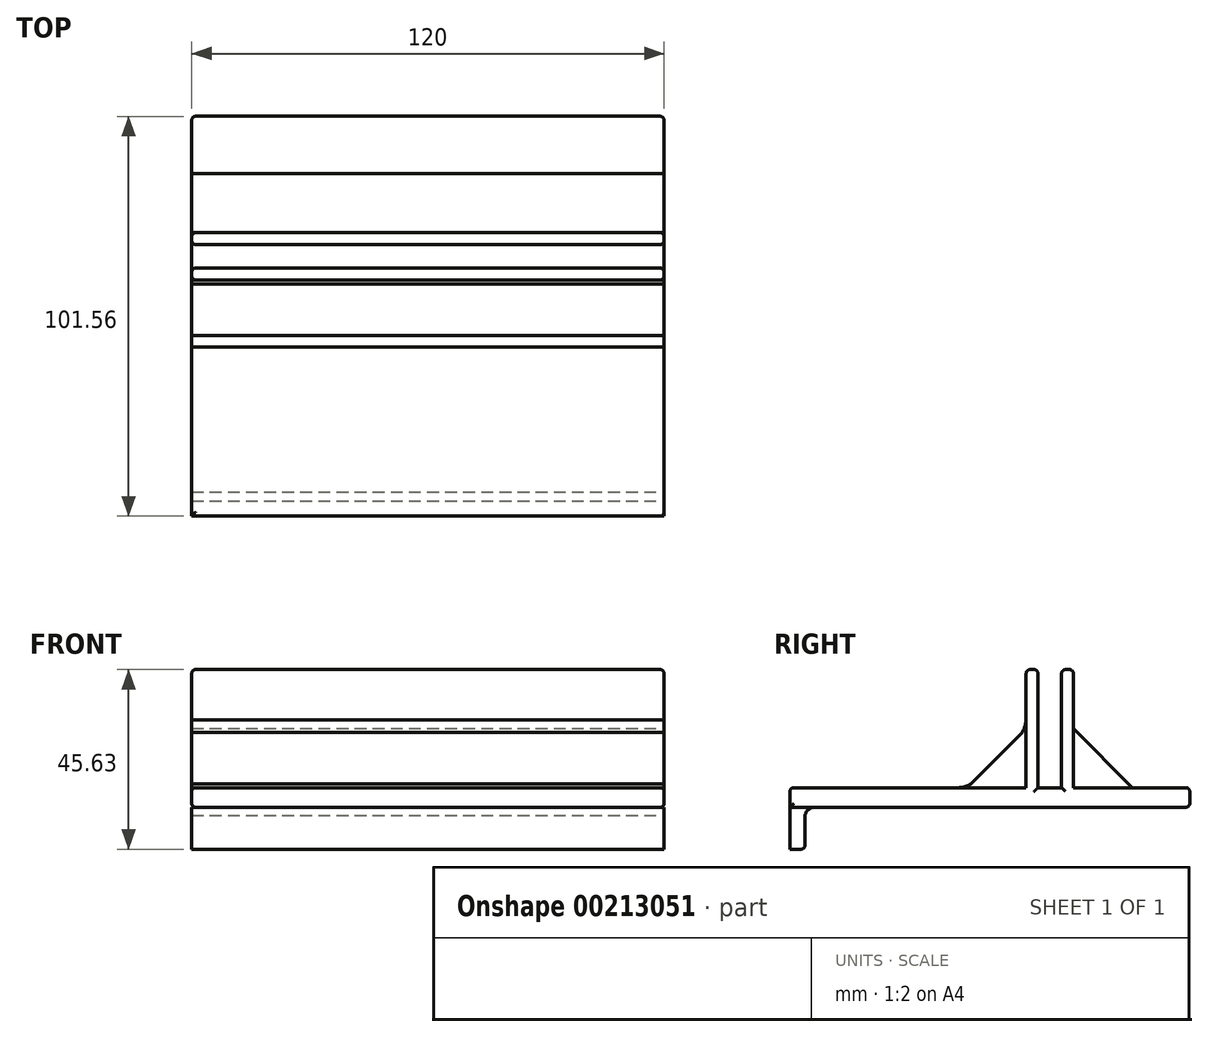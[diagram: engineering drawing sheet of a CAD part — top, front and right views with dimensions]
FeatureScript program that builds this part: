
annotation { "Feature Type Name" : "Feature", "Feature Type Description" : "" }
export const myFeature = defineFeature(function(context is Context, id is Id, definition is map)
    precondition{}
    {
        {
            var Q0;
            Q0=qCreatedBy(makeId("Top.planeOp"),FACE);
            var sketch = newSketch(context, id + "F0", { "sketchPlane" : qUnion([Q0])});
            skLineSegment(sketch, "E0.bottom", {"start": v(60, 66) * mm, "end": v(-60, 66) * mm});
            skLineSegment(sketch, "E0.top", {"start": v(60, -66) * mm, "end": v(-60, -66) * mm});
            skLineSegment(sketch, "E0.left", {"start": v(60, 66) * mm, "end": v(60, -66) * mm});
            skLineSegment(sketch, "E0.right", {"start": v(-60, 66) * mm, "end": v(-60, -66) * mm});
            skPoint(sketch, "E0.middle", {"position": v(0, 0) * mm});
            skSolve(sketch);
        }
        {
            var Q0;
            Q0=makeQuery(id+"F0.imprint","IMPRINT",FACE,{"disambiguationData":[TD([[makeQuery(id+"F0.imprint","IMPRINT",EDGE,{"derivedFrom":sQuery(id+"F0.wireOp",EDGE,"E0.bottom")}),1.0]])]});
            extrude(context, id + "F1", {"entities" : qUnion([Q0]), "depth" : 5 * mm});
        }
        {
            var Q0;
            Q0=makeQuery(id+"F1.opExtrude","CAP_FACE",FACE,{"disambiguationData":[OSD([sQuery(id+"F0.wireOp",EDGE,"E0.bottom"),sQuery(id+"F0.wireOp",EDGE,"E0.top"),sQuery(id+"F0.wireOp",EDGE,"E0.left"),sQuery(id+"F0.wireOp",EDGE,"E0.right")])],"isStart":false});
            var sketch = newSketch(context, id + "F2", { "sketchPlane" : qUnion([Q0])});
            skLineSegment(sketch, "E1.bottom", {"start": v(60, 6) * mm, "end": v(-60, 6) * mm});
            skLineSegment(sketch, "E1.top", {"start": v(60, -6) * mm, "end": v(-60, -6) * mm});
            skLineSegment(sketch, "E1.left", {"start": v(60, 6) * mm, "end": v(60, -6) * mm});
            skLineSegment(sketch, "E1.right", {"start": v(-60, 6) * mm, "end": v(-60, -6) * mm});
            skPoint(sketch, "E1.middle", {"position": v(0, 0) * mm});
            skLineSegment(sketch, "E2", {"start": v(-60, 3) * mm, "end": v(60, 3) * mm});
            skLineSegment(sketch, "E3", {"start": v(-60, -3) * mm, "end": v(60, -3) * mm});
            skSolve(sketch);
        }
        {
            var Q0;
            {var subQ0=sQuery(id+"F2.wireOp",EDGE,"E1.bottom");Q0=makeQuery(id+"F2.imprint","IMPRINT",FACE,{"disambiguationData":[TD([[makeQuery(id+"F2.imprint","IMPRINT",EDGE,{"derivedFrom":subQ0}),1.0]])]});}
            var Q1;
            {var subQ0=sQuery(id+"F2.wireOp",EDGE,"E1.top");Q1=makeQuery(id+"F2.imprint","IMPRINT",FACE,{"disambiguationData":[TD([[makeQuery(id+"F2.imprint","IMPRINT",EDGE,{"derivedFrom":subQ0}),-1.0]])]});}
            extrude(context, id + "F3", {"entities" : qUnion([Q0, Q1]), "operationType" : NewBodyOperationType.ADD, "depth" : 30 * mm});
        }
        {
            var Q0;
            {var subQ0=sQuery(id+"F2.wireOp",EDGE,"E1.left");var subQ1=sQuery(id+"F0.wireOp",EDGE,"E0.left");Q0=makeQuery(id+"F3.boolean.opBoolean","MERGE",FACE,{"derivedFrom":[makeQuery(id+"F1.opExtrude","SWEPT_FACE",FACE,{"disambiguationData":[OSD([subQ1])]}),makeQuery(id+"F3.opExtrude","SWEPT_FACE",FACE,{"disambiguationData":[OSD([subQ0]),TDD([makeQuery(id+"F2.imprint","IMPRINT",EDGE,{"disambiguationData":[TD([[makeQuery(id+"F2.imprint","INTERSECT",VERTEX,{"derivedFrom":[subQ0,sQuery(id+"F2.wireOp",EDGE,"E2")]}),1.0]])],"derivedFrom":subQ0})])]}),makeQuery(id+"F3.opExtrude","SWEPT_FACE",FACE,{"disambiguationData":[OSD([subQ0]),TDD([makeQuery(id+"F2.imprint","IMPRINT",EDGE,{"disambiguationData":[TD([[makeQuery(id+"F2.imprint","INTERSECT",VERTEX,{"derivedFrom":[subQ0,sQuery(id+"F2.wireOp",EDGE,"E3")]}),-1.0]])],"derivedFrom":subQ0})])]})]});}
            var sketch = newSketch(context, id + "F4", { "sketchPlane" : qUnion([Q0])});
            skLineSegment(sketch, "E4", {"start": v(-21, 5) * mm, "end": v(-6, 20) * mm});
            skLineSegment(sketch, "E5", {"start": v(21, 5) * mm, "end": v(6, 20) * mm});
            skLineSegment(sketch, "E6.bottom", {"start": v(-66, 0) * mm, "end": v(-62.19, 0) * mm});
            skLineSegment(sketch, "E6.top", {"start": v(-66, -10.63) * mm, "end": v(-62.19, -10.63) * mm});
            skLineSegment(sketch, "E6.left", {"start": v(-66, 0) * mm, "end": v(-66, -10.63) * mm});
            skLineSegment(sketch, "E6.right", {"start": v(-62.19, 0) * mm, "end": v(-62.19, -10.63) * mm});
            skArc(sketch, "E7", {"start": v(-7.02, 18.98) * mm, "mid": v(-6.36, 20.56) * mm, "end": v(-6, 22.23) * mm});
            skArc(sketch, "E8", {"start": v(-23.04, 5) * mm, "mid": v(-21.5, 5.27) * mm, "end": v(-20.1, 5.9) * mm});
            skArc(sketch, "E9", {"start": v(-59.92, 0) * mm, "mid": v(-61.38, -0.65) * mm, "end": v(-62.19, -2.01) * mm});
            skLineSegment(sketch, "E10", {"start": v(0, 5) * mm, "end": v(0, 31.5) * mm});
            skPoint(sketch, "E10.endSnap0", {"position": v(0, 5) * mm});
            skArc(sketch, "E11.MirrorCS", {"start": v(7.02, 18.98) * mm, "mid": v(6.36, 20.56) * mm, "end": v(6, 22.23) * mm});
            skArc(sketch, "E12.MirrorCS", {"start": v(23.04, 5) * mm, "mid": v(21.5, 5.27) * mm, "end": v(20.1, 5.9) * mm});
            skSolve(sketch);
        }
        {
            var Q0;
            {var subQ0=sQuery(id+"F4.wireOp",EDGE,"E4");Q0=makeQuery(id+"F4.imprint","IMPRINT",FACE,{"disambiguationData":[TD([[makeQuery(id+"F4.imprint","IMPRINT",EDGE,{"derivedFrom":subQ0}),-1.0]])]});}
            var Q1;
            {var subQ0=sQuery(id+"F4.wireOp",EDGE,"E5");Q1=makeQuery(id+"F4.imprint","IMPRINT",FACE,{"disambiguationData":[TD([[makeQuery(id+"F4.imprint","IMPRINT",EDGE,{"derivedFrom":subQ0}),1.0]])]});}
            var Q2;
            Q2=makeQuery(id+"F4.imprint","IMPRINT",FACE,{"disambiguationData":[TD([[makeQuery(id+"F4.imprint","IMPRINT",EDGE,{"derivedFrom":sQuery(id+"F4.wireOp",EDGE,"E6.bottom")}),1.0]])]});
            var Q3;
            {var subQ3=sQuery(id+"F4.wireOp",EDGE,"E7");Q3=makeQuery(id+"F4.imprint","IMPRINT",FACE,{"disambiguationData":[TD([[makeQuery(id+"F4.imprint","IMPRINT",EDGE,{"derivedFrom":subQ3}),-1.0]])]});}
            var Q4;
            {var subQ3=sQuery(id+"F4.wireOp",EDGE,"E11.MirrorCS");Q4=makeQuery(id+"F4.imprint","IMPRINT",FACE,{"disambiguationData":[TD([[makeQuery(id+"F4.imprint","IMPRINT",EDGE,{"derivedFrom":subQ3}),1.0]])]});}
            var Q5;
            {var subQ8=sQuery(id+"F4.wireOp",EDGE,"E8");Q5=makeQuery(id+"F4.imprint","IMPRINT",FACE,{"disambiguationData":[TD([[makeQuery(id+"F4.imprint","IMPRINT",EDGE,{"derivedFrom":subQ8}),-1.0]])]});}
            var Q6;
            {var subQ8=sQuery(id+"F4.wireOp",EDGE,"E12.MirrorCS");Q6=makeQuery(id+"F4.imprint","IMPRINT",FACE,{"disambiguationData":[TD([[makeQuery(id+"F4.imprint","IMPRINT",EDGE,{"derivedFrom":subQ8}),1.0]])]});}
            var Q7;
            {var subQ3=sQuery(id+"F4.wireOp",EDGE,"E9");Q7=makeQuery(id+"F4.imprint","IMPRINT",FACE,{"disambiguationData":[TD([[makeQuery(id+"F4.imprint","IMPRINT",EDGE,{"derivedFrom":subQ3}),-1.0]])]});}
            extrude(context, id + "F5", {"entities" : qUnion([Q0, Q1, Q2, Q3, Q4, Q5, Q6, Q7]), "oppositeDirection" : true, "depth" : 120 * mm});
        }
        {
            var Q0;
            {var subQ0=sQuery(id+"F2.wireOp",EDGE,"E1.left");var subQ1=sQuery(id+"F0.wireOp",EDGE,"E0.left");Q0=makeQuery(id+"F3.boolean.opBoolean","MERGE",FACE,{"derivedFrom":[makeQuery(id+"F1.opExtrude","SWEPT_FACE",FACE,{"disambiguationData":[OSD([subQ1])]}),makeQuery(id+"F3.opExtrude","SWEPT_FACE",FACE,{"disambiguationData":[OSD([subQ0]),TDD([makeQuery(id+"F2.imprint","IMPRINT",EDGE,{"disambiguationData":[TD([[makeQuery(id+"F2.imprint","INTERSECT",VERTEX,{"derivedFrom":[subQ0,sQuery(id+"F2.wireOp",EDGE,"E2")]}),1.0]])],"derivedFrom":subQ0})])]}),makeQuery(id+"F3.opExtrude","SWEPT_FACE",FACE,{"disambiguationData":[OSD([subQ0]),TDD([makeQuery(id+"F2.imprint","IMPRINT",EDGE,{"disambiguationData":[TD([[makeQuery(id+"F2.imprint","INTERSECT",VERTEX,{"derivedFrom":[subQ0,sQuery(id+"F2.wireOp",EDGE,"E3")]}),-1.0]])],"derivedFrom":subQ0})])]})]});}
            var Q1;
            {var subQ0=sQuery(id+"F0.wireOp",EDGE,"E0.right");var subQ2=sQuery(id+"F0.wireOp",EDGE,"E0.left");var subQ3=sQuery(id+"F0.wireOp",EDGE,"E0.bottom");Q1=makeQuery(id+"F3.boolean.opBoolean","SPLIT",FACE,{"disambiguationData":[TD([makeQuery(id+"F1.opExtrude","SWEPT_FACE",FACE,{"disambiguationData":[OSD([subQ3])]})])],"derivedFrom":makeQuery(id+"F1.opExtrude","CAP_FACE",FACE,{"disambiguationData":[OSD([subQ3,sQuery(id+"F0.wireOp",EDGE,"E0.top"),subQ2,subQ0])],"isStart":false})});}
            var Q2;
            {var subQ1=sQuery(id+"F0.wireOp",EDGE,"E0.right");var subQ2=sQuery(id+"F0.wireOp",EDGE,"E0.left");var subQ3=sQuery(id+"F0.wireOp",EDGE,"E0.top");Q2=makeQuery(id+"F3.boolean.opBoolean","SPLIT",FACE,{"disambiguationData":[TD([makeQuery(id+"F1.opExtrude","SWEPT_FACE",FACE,{"disambiguationData":[OSD([subQ3])]})])],"derivedFrom":makeQuery(id+"F1.opExtrude","CAP_FACE",FACE,{"disambiguationData":[OSD([sQuery(id+"F0.wireOp",EDGE,"E0.bottom"),subQ3,subQ2,subQ1])],"isStart":false})});}
            var Q3;
            Q3=makeQuery(id+"F3.opExtrude","CAP_EDGE",EDGE,{"disambiguationData":[OSD([sQuery(id+"F2.wireOp",EDGE,"E1.top")])],"isStart":false});
            var Q4;
            Q4=makeQuery(id+"F3.opExtrude","CAP_EDGE",EDGE,{"disambiguationData":[OSD([sQuery(id+"F2.wireOp",EDGE,"E3")])],"isStart":false});
            var Q5;
            Q5=makeQuery(id+"F3.opExtrude","CAP_EDGE",EDGE,{"disambiguationData":[OSD([sQuery(id+"F2.wireOp",EDGE,"E1.bottom")])],"isStart":false});
            var Q6;
            Q6=makeQuery(id+"F3.opExtrude","CAP_EDGE",EDGE,{"disambiguationData":[OSD([sQuery(id+"F2.wireOp",EDGE,"E2")])],"isStart":false});
            var Q7;
            Q7=makeQuery(id+"F5.opExtrude","CAP_EDGE",EDGE,{"disambiguationData":[OSD([sQuery(id+"F4.wireOp",EDGE,"E6.left")])],"isStart":false});
            var Q8;
            Q8=makeQuery(id+"F5.opExtrude","SWEPT_EDGE",EDGE,{"disambiguationData":[OSD([sQuery(id+"F4.wireOp",EDGE,"E6.top"),sQuery(id+"F4.wireOp",EDGE,"E6.right")])]});
            var Q9;
            Q9=makeQuery(id+"F1.opExtrude","CAP_EDGE",EDGE,{"disambiguationData":[OSD([sQuery(id+"F0.wireOp",EDGE,"E0.right")])],"isStart":true});
            var Q10;
            Q10=makeQuery(id+"F1.opExtrude","CAP_EDGE",EDGE,{"disambiguationData":[OSD([sQuery(id+"F0.wireOp",EDGE,"E0.bottom")])],"isStart":true});
            var Q11;
            Q11=makeQuery(id+"F1.opExtrude","SWEPT_EDGE",EDGE,{"disambiguationData":[OSD([sQuery(id+"F0.wireOp",EDGE,"E0.bottom"),sQuery(id+"F0.wireOp",EDGE,"E0.right")])]});
            fillet(context, id + "F6", {"entities" : qUnion([Q0, Q1, Q2, Q3, Q4, Q5, Q6, Q7, Q8, Q9, Q10, Q11]), "radius" : 1 * mm, "tangentPropagation" : true, "allowEdgeOverflow" : false});
        }
        {
            var Q0;
            {var subQ1=sQuery(id+"F0.wireOp",EDGE,"E0.right");var subQ2=makeQuery(id+"F1.opExtrude","CAP_EDGE",EDGE,{"disambiguationData":[OSD([subQ1])],"isStart":false});var subQ4=sQuery(id+"F2.wireOp",EDGE,"E2");Q0=makeQuery(id+"F3.boolean.opBoolean","SPLIT",EDGE,{"disambiguationData":[TD([makeQuery(id+"F3.opExtrude","SWEPT_FACE",FACE,{"disambiguationData":[OSD([subQ4])]})])],"derivedFrom":subQ2});}
            fillet(context, id + "F7", {"entities" : qUnion([Q0]), "radius" : 1 * mm, "tangentPropagation" : true, "allowEdgeOverflow" : false});
        }
        {
            var Q0;
            Q0=makeQuery(id+"F3.opExtrude","SWEPT_EDGE",EDGE,{"disambiguationData":[OSD([sQuery(id+"F2.wireOp",EDGE,"E1.right"),sQuery(id+"F2.wireOp",EDGE,"E2")])]});
            var Q1;
            Q1=makeQuery(id+"F3.opExtrude","SWEPT_EDGE",EDGE,{"disambiguationData":[OSD([sQuery(id+"F2.wireOp",EDGE,"E1.right"),sQuery(id+"F2.wireOp",EDGE,"E3")])]});
            fillet(context, id + "F8", {"entities" : qUnion([Q0, Q1]), "radius" : 1 * mm, "tangentPropagation" : true, "allowEdgeOverflow" : false});
        }
        {
            var Q0;
            {var subQ0=sQuery(id+"F0.wireOp",EDGE,"E0.right");var subQ2=sQuery(id+"F0.wireOp",EDGE,"E0.left");var subQ3=sQuery(id+"F0.wireOp",EDGE,"E0.bottom");Q0=makeQuery(id+"F3.boolean.opBoolean","SPLIT",FACE,{"disambiguationData":[TD([makeQuery(id+"F1.opExtrude","SWEPT_FACE",FACE,{"disambiguationData":[OSD([subQ3])]})])],"derivedFrom":makeQuery(id+"F1.opExtrude","CAP_FACE",FACE,{"disambiguationData":[OSD([subQ3,sQuery(id+"F0.wireOp",EDGE,"E0.top"),subQ2,subQ0])],"isStart":false})});}
            var sketch = newSketch(context, id + "F9", { "sketchPlane" : qUnion([Q0])});
            skLineSegment(sketch, "E13.bottom", {"start": v(-67.37, 35.56) * mm, "end": v(70.59, 35.56) * mm});
            skLineSegment(sketch, "E13.top", {"start": v(-67.37, 72.86) * mm, "end": v(70.59, 72.86) * mm});
            skLineSegment(sketch, "E13.left", {"start": v(-67.37, 35.56) * mm, "end": v(-67.37, 72.86) * mm});
            skLineSegment(sketch, "E13.right", {"start": v(70.59, 35.56) * mm, "end": v(70.59, 72.86) * mm});
            skSolve(sketch);
        }
        {
            var Q0;
            Q0=makeQuery(id+"F9.imprint","IMPRINT",FACE,{"disambiguationData":[TD([[makeQuery(id+"F9.imprint","IMPRINT",EDGE,{"derivedFrom":sQuery(id+"F9.wireOp",EDGE,"E13.top")}),-1.0]])]});
            var Q1;
            {var subQ1=sQuery(id+"F0.wireOp",EDGE,"E0.right");var subQ5=sQuery(id+"F0.wireOp",EDGE,"E0.left");var subQ7=sQuery(id+"F0.wireOp",EDGE,"E0.bottom");var subQ8=makeQuery(id+"F1.opExtrude","SWEPT_FACE",FACE,{"disambiguationData":[OSD([subQ7])]});var subQ20=makeQuery(id+"F1.opExtrude","CAP_FACE",FACE,{"disambiguationData":[OSD([subQ7,sQuery(id+"F0.wireOp",EDGE,"E0.top"),subQ5,subQ1])],"isStart":false});var subQ21=makeQuery(id+"F3.boolean.opBoolean","SPLIT",FACE,{"disambiguationData":[TD([subQ8])],"derivedFrom":subQ20});var subQ26=makeQuery(id+"F6.opFillet","BLEND_EDGE",EDGE,{"blendedFrom":[makeQuery(id+"F1.opExtrude","CAP_EDGE",EDGE,{"disambiguationData":[OSD([subQ7])],"isStart":false}),subQ21],"blendedInto":[subQ21]});Q1=makeQuery(id+"F9.imprint","IMPRINT",FACE,{"disambiguationData":[TD([[makeQuery(id+"F9.imprint","IMPRINT",EDGE,{"derivedFrom":subQ26}),1.0]])]});}
            extrude(context, id + "F10", {"entities" : qUnion([Q0, Q1]), "operationType" : NewBodyOperationType.REMOVE, "oppositeDirection" : true, "depth" : 25 * mm});
        }
        {
            var Q0;
            Q0=makeQuery(id+"F10.boolean.opBoolean","COPY",EDGE,{"derivedFrom":makeQuery(id+"F10.opExtrude","CAP_EDGE",EDGE,{"disambiguationData":[OSD([sQuery(id+"F9.wireOp",EDGE,"E13.bottom")])],"isStart":true})});
            var Q1;
            Q1=makeQuery(id+"F10.boolean.opBoolean","INTERSECT",EDGE,{"derivedFrom":[makeQuery(id+"F1.opExtrude","CAP_FACE",FACE,{"disambiguationData":[OSD([sQuery(id+"F0.wireOp",EDGE,"E0.bottom"),sQuery(id+"F0.wireOp",EDGE,"E0.top"),sQuery(id+"F0.wireOp",EDGE,"E0.left"),sQuery(id+"F0.wireOp",EDGE,"E0.right")])],"isStart":true}),makeQuery(id+"F10.opExtrude","SWEPT_FACE",FACE,{"disambiguationData":[OSD([sQuery(id+"F9.wireOp",EDGE,"E13.bottom")])]})]});
            fillet(context, id + "F11", {"entities" : qUnion([Q0, Q1]), "radius" : 1 * mm, "tangentPropagation" : true, "allowEdgeOverflow" : false});
        }
    });
